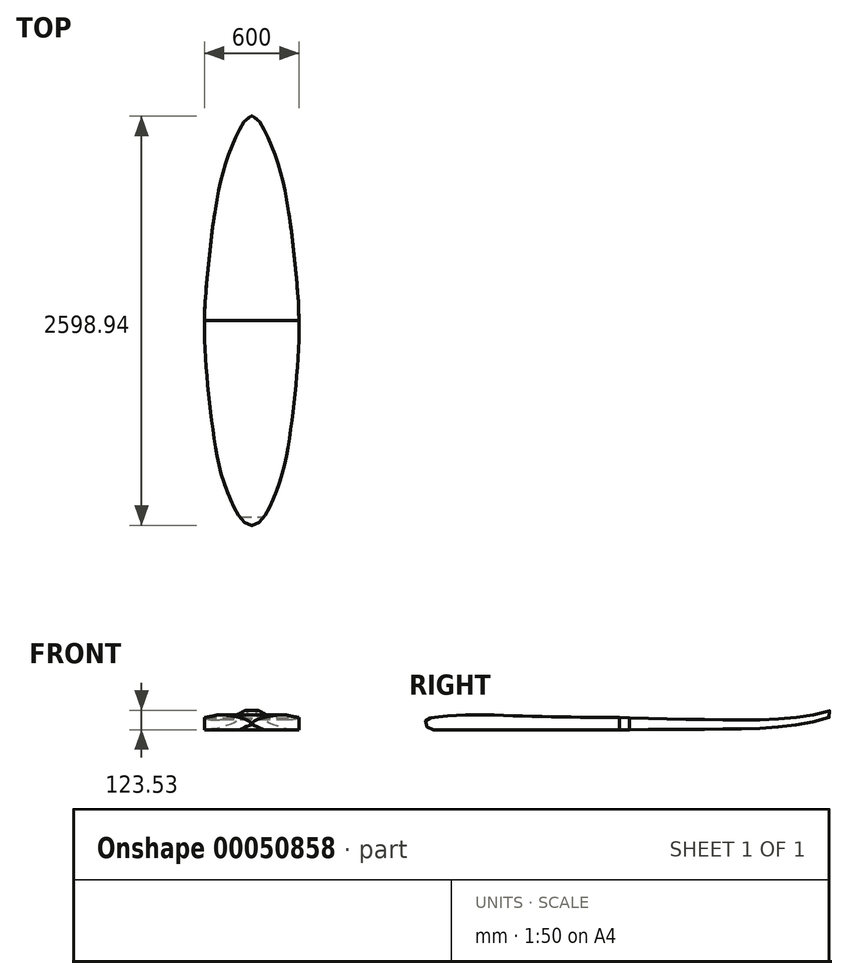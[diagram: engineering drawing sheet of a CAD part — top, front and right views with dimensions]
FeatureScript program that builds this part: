
annotation { "Feature Type Name" : "Feature", "Feature Type Description" : "" }
export const myFeature = defineFeature(function(context is Context, id is Id, definition is map)
    precondition{}
    {
        {
            var Q0;
            Q0=qCreatedBy(makeId("Top.planeOp"),FACE);
            var sketch = newSketch(context, id + "F0", { "sketchPlane" : qUnion([Q0])});
            skLineSegment(sketch, "E0.rect.bottom", {"start": v(300, 1300) * mm, "end": v(-300, 1300) * mm});
            skLineSegment(sketch, "E0.rect.top", {"start": v(300, -1300) * mm, "end": v(-300, -1300) * mm});
            skLineSegment(sketch, "E0.rect.left", {"start": v(300, 1300) * mm, "end": v(300, -1300) * mm});
            skLineSegment(sketch, "E0.rect.right", {"start": v(-300, 1300) * mm, "end": v(-300, -1300) * mm});
            skPoint(sketch, "E0.rect.middle", {"position": v(0, 0) * mm});
            skLineSegment(sketch, "E1", {"start": v(0, 1300) * mm, "end": v(0, -1300) * mm, "construction": true});
            skLineSegment(sketch, "E2", {"start": v(-300, 0) * mm, "end": v(300, 0) * mm, "construction": true});
            skSolve(sketch);
        }
        {
            var Q0;
            Q0=makeQuery(id+"F0.imprint","IMPRINT",FACE,{"disambiguationData":[TD([[makeQuery(id+"F0.imprint","IMPRINT",EDGE,{"derivedFrom":sQuery(id+"F0.wireOp",EDGE,"E0.rect.bottom")}),1.0]])]});
            extrude(context, id + "F1", {"entities" : qUnion([Q0]), "depth" : 152.4 * mm});
        }
        {
            var Q0;
            Q0=makeQuery(id+"F1.opExtrude","CAP_FACE",FACE,{"disambiguationData":[OSD([sQuery(id+"F0.wireOp",EDGE,"E0.rect.bottom"),sQuery(id+"F0.wireOp",EDGE,"E0.rect.top"),sQuery(id+"F0.wireOp",EDGE,"E0.rect.left"),sQuery(id+"F0.wireOp",EDGE,"E0.rect.right")])],"isStart":false});
            var sketch = newSketch(context, id + "F2", { "sketchPlane" : qUnion([Q0])});
            skLineSegment(sketch, "E3.rect.bottom", {"start": v(300, 1300) * mm, "end": v(-300, 1300) * mm});
            skLineSegment(sketch, "E3.rect.top", {"start": v(300, -1300) * mm, "end": v(-300, -1300) * mm});
            skLineSegment(sketch, "E3.rect.left", {"start": v(300, 1300) * mm, "end": v(300, -1300) * mm});
            skLineSegment(sketch, "E3.rect.right", {"start": v(-300, 1300) * mm, "end": v(-300, -1300) * mm});
            skPoint(sketch, "E3.rect.middle", {"position": v(0, 0) * mm});
            skLineSegment(sketch, "E4", {"start": v(0, 1300) * mm, "end": v(0, -1300) * mm, "construction": true});
            skLineSegment(sketch, "E5", {"start": v(-300, 0) * mm, "end": v(300, 0) * mm, "construction": true});
            skFitSpline(sketch, "E6", {"points": [v(0, 1300) * mm, v(-23.46, 1292.92) * mm, v(-51.5, 1259.74) * mm, v(-112.1, 1144.2) * mm, v(-207.16, 841) * mm, v(-274.14, 365.24) * mm, v(-300, 0) * mm, v(-278.48, -420.31) * mm, v(-213.54, -890.24) * mm, v(-145.66, -1113.28) * mm, v(-83.55, -1236.46) * mm, v(-37.46, -1286.72) * mm, v(0, -1300) * mm], "startDerivative": vector(-810.7, -129.8) * mm, "endDerivative": vector(997.29, -228.98) * mm});
            skFitSpline(sketch, "E7.MirrorCS", {"points": [v(0, 1300) * mm, v(23.46, 1292.92) * mm, v(51.5, 1259.74) * mm, v(112.1, 1144.2) * mm, v(207.16, 841) * mm, v(274.14, 365.24) * mm, v(300, 0) * mm, v(278.48, -420.31) * mm, v(213.54, -890.24) * mm, v(145.66, -1113.28) * mm, v(83.55, -1236.46) * mm, v(37.46, -1286.72) * mm, v(0, -1300) * mm], "startDerivative": vector(810.7, -129.8) * mm, "endDerivative": vector(-997.29, -228.98) * mm});
            skSolve(sketch);
        }
        {
            var Q0;
            {var subQ0=sQuery(id+"F2.wireOp",EDGE,"E3.rect.right");var subQ1=sQuery(id+"F2.wireOp",EDGE,"E3.rect.top");var subQ2=makeQuery(id+"F2.imprint","INTERSECT",VERTEX,{"derivedFrom":[subQ1,subQ0]});Q0=makeQuery(id+"F2.imprint","IMPRINT",FACE,{"disambiguationData":[TD([[makeQuery(id+"F2.imprint","IMPRINT",EDGE,{"disambiguationData":[TD([[subQ2,1.0]])],"derivedFrom":subQ0}),1.0]])]});}
            var Q1;
            {var subQ0=sQuery(id+"F2.wireOp",EDGE,"E3.rect.right");var subQ1=sQuery(id+"F2.wireOp",EDGE,"E3.rect.bottom");var subQ2=makeQuery(id+"F2.imprint","INTERSECT",VERTEX,{"derivedFrom":[subQ1,subQ0]});Q1=makeQuery(id+"F2.imprint","IMPRINT",FACE,{"disambiguationData":[TD([[makeQuery(id+"F2.imprint","IMPRINT",EDGE,{"disambiguationData":[TD([[subQ2,-1.0]])],"derivedFrom":subQ0}),1.0]])]});}
            var Q2;
            {var subQ0=sQuery(id+"F2.wireOp",EDGE,"E3.rect.left");var subQ1=sQuery(id+"F2.wireOp",EDGE,"E3.rect.bottom");var subQ2=makeQuery(id+"F2.imprint","INTERSECT",VERTEX,{"derivedFrom":[subQ1,subQ0]});Q2=makeQuery(id+"F2.imprint","IMPRINT",FACE,{"disambiguationData":[TD([[makeQuery(id+"F2.imprint","IMPRINT",EDGE,{"disambiguationData":[TD([[subQ2,-1.0]])],"derivedFrom":subQ0}),-1.0]])]});}
            var Q3;
            {var subQ0=sQuery(id+"F2.wireOp",EDGE,"E3.rect.left");var subQ1=sQuery(id+"F2.wireOp",EDGE,"E3.rect.top");var subQ2=makeQuery(id+"F2.imprint","INTERSECT",VERTEX,{"derivedFrom":[subQ1,subQ0]});Q3=makeQuery(id+"F2.imprint","IMPRINT",FACE,{"disambiguationData":[TD([[makeQuery(id+"F2.imprint","IMPRINT",EDGE,{"disambiguationData":[TD([[subQ2,1.0]])],"derivedFrom":subQ0}),-1.0]])]});}
            extrude(context, id + "F3", {"entities" : qUnion([Q0, Q1, Q2, Q3]), "operationType" : NewBodyOperationType.REMOVE, "endBound" : BoundingType.THROUGH_ALL, "oppositeDirection" : true, "depth" : 25.4 * mm});
        }
        {
            var Q0;
            Q0=makeQuery(id+"F1.opExtrude","SWEPT_FACE",FACE,{"disambiguationData":[OSD([sQuery(id+"F0.wireOp",EDGE,"E0.rect.left")])]});
            var sketch = newSketch(context, id + "F4", { "sketchPlane" : qUnion([Q0])});
            skLineSegment(sketch, "E8.bottom", {"start": v(0, 0) * mm, "end": v(1338.36, 0) * mm});
            skLineSegment(sketch, "E8.top", {"start": v(0, 152.4) * mm, "end": v(1338.36, 152.4) * mm});
            skLineSegment(sketch, "E8.left", {"start": v(0, 0) * mm, "end": v(0, 152.4) * mm});
            skLineSegment(sketch, "E8.right", {"start": v(1338.36, 0) * mm, "end": v(1338.36, 152.4) * mm});
            skFitSpline(sketch, "E9", {"points": [v(0, 0) * mm, v(587.46, 4.47) * mm, v(962.53, 19.46) * mm, v(1193.43, 56.02) * mm, v(1257.6, 74.9) * mm, v(1292.5, 94.35) * mm, v(1298.21, 116.66) * mm, v(1285.06, 123.53) * mm, v(1242.72, 112.66) * mm, v(1188.95, 97.21) * mm, v(955.3, 68.87) * mm, v(585.44, 62.45) * mm, v(0, 76.2) * mm], "startDerivative": vector(3940.11, 21.2) * mm, "endDerivative": vector(-3947.88, 113.17) * mm});
            skSolve(sketch);
        }
        {
            var Q0;
            Q0=makeQuery(id+"F4.imprint","IMPRINT",FACE,{"disambiguationData":[TD([[makeQuery(id+"F4.imprint","IMPRINT",EDGE,{"derivedFrom":sQuery(id+"F4.wireOp",EDGE,"E8.bottom")}),1.0]])]});
            extrude(context, id + "F5", {"entities" : qUnion([Q0]), "operationType" : NewBodyOperationType.REMOVE, "endBound" : BoundingType.THROUGH_ALL, "oppositeDirection" : true, "depth" : 25.4 * mm});
        }
        {
            var Q0;
            Q0=makeQuery(id+"F1.opExtrude","SWEPT_FACE",FACE,{"disambiguationData":[OSD([sQuery(id+"F0.wireOp",EDGE,"E0.rect.left")])]});
            var sketch = newSketch(context, id + "F6", { "sketchPlane" : qUnion([Q0])});
            skLineSegment(sketch, "E10.bottom", {"start": v(0, 0) * mm, "end": v(-1311.25, 0) * mm});
            skLineSegment(sketch, "E10.top", {"start": v(0, 169.85) * mm, "end": v(-1311.25, 169.85) * mm});
            skLineSegment(sketch, "E10.left", {"start": v(0, 0) * mm, "end": v(0, 169.85) * mm});
            skLineSegment(sketch, "E10.right", {"start": v(-1311.25, 0) * mm, "end": v(-1311.25, 169.85) * mm});
            skFitSpline(sketch, "E11", {"points": [v(0, 76.2) * mm, v(-694.68, 87.11) * mm, v(-1044.4, 93.88) * mm, v(-1255.16, 76.2) * mm, v(-1280.75, 68.24) * mm, v(-1295.78, 56.45) * mm, v(-1297.5, 29) * mm, v(-1283.2, 15.26) * mm, v(-1246.01, 0) * mm], "startDerivative": vector(-2439.45, 27.14) * mm, "endDerivative": vector(1305.95, -395.5) * mm});
            skSolve(sketch);
        }
        {
            var Q0;
            {var subQ2=sQuery(id+"F6.wireOp",EDGE,"E10.top");Q0=makeQuery(id+"F6.imprint","IMPRINT",FACE,{"disambiguationData":[TD([[makeQuery(id+"F6.imprint","IMPRINT",EDGE,{"derivedFrom":subQ2}),1.0]])]});}
            extrude(context, id + "F7", {"entities" : qUnion([Q0]), "operationType" : NewBodyOperationType.REMOVE, "endBound" : BoundingType.THROUGH_ALL, "oppositeDirection" : true, "depth" : 25.4 * mm});
        }
        {
            var Q0;
            Q0=makeQuery(id+"F1.opExtrude","SWEPT_FACE",FACE,{"disambiguationData":[OSD([sQuery(id+"F0.wireOp",EDGE,"E0.rect.left")])]});
            var sketch = newSketch(context, id + "F8", { "sketchPlane" : qUnion([Q0])});
            skLineSegment(sketch, "E12", {"start": v(-65.22, 76.92) * mm, "end": v(0, 76.2) * mm});
            skSolve(sketch);
        }
        {
            var Q0;
            Q0 = qSketchRegion(id + "F8", true);
            var Q1;
            Q1=makeQuery(id+"F8.imprint","IMPRINT",FACE,{"disambiguationData":[TD([[makeQuery(id+"F8.imprint","IMPRINT",EDGE,{"derivedFrom":sQuery(id+"F8.wireOp",EDGE,"E12")}),1.0]])]});
            extrude(context, id + "F9", {"entities" : qUnion([Q0, Q1]), "operationType" : NewBodyOperationType.REMOVE, "endBound" : BoundingType.THROUGH_ALL, "oppositeDirection" : true, "depth" : 25.4 * mm});
        }
    });
